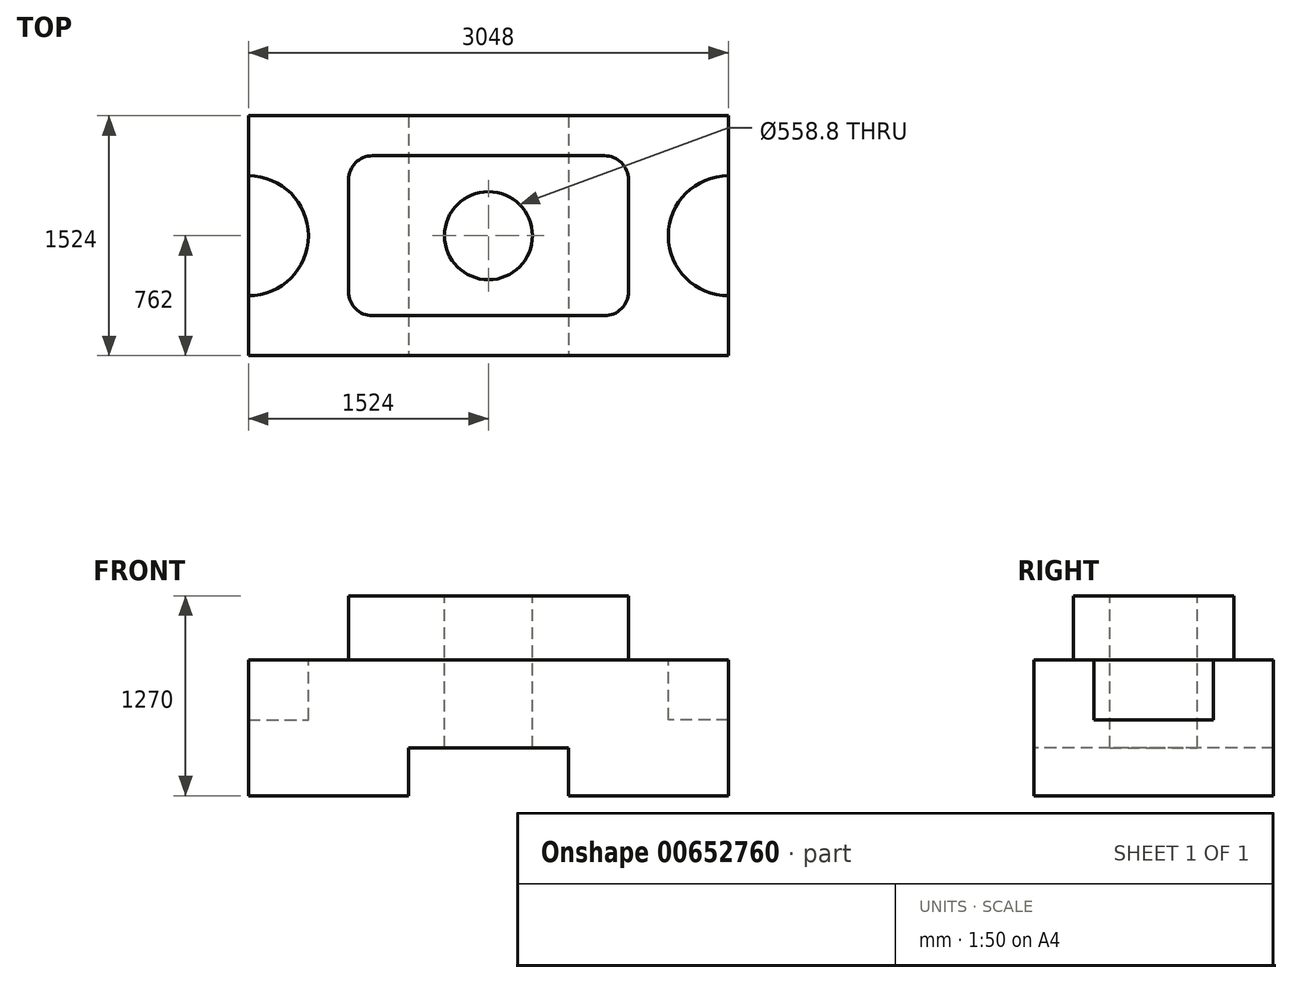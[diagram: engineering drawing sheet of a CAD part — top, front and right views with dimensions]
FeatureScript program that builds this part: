
annotation { "Feature Type Name" : "Feature", "Feature Type Description" : "" }
export const myFeature = defineFeature(function(context is Context, id is Id, definition is map)
    precondition{}
    {
        {
            var Q0;
            Q0=qCreatedBy(makeId("Top.planeOp"),FACE);
            var sketch = newSketch(context, id + "F0", { "sketchPlane" : qUnion([Q0])});
            skLineSegment(sketch, "E0.bottom", {"start": v(1524, -762) * mm, "end": v(-1524, -762) * mm});
            skLineSegment(sketch, "E0.top", {"start": v(1524, 762) * mm, "end": v(-1524, 762) * mm});
            skLineSegment(sketch, "E0.left", {"start": v(1524, -762) * mm, "end": v(1524, 762) * mm});
            skLineSegment(sketch, "E0.right", {"start": v(-1524, -762) * mm, "end": v(-1524, 762) * mm});
            skPoint(sketch, "E0.middle", {"position": v(0, 0) * mm});
            skSolve(sketch);
        }
        {
            var Q0;
            Q0=makeQuery(id+"F0.imprint","IMPRINT",FACE,{"disambiguationData":[TD([[makeQuery(id+"F0.imprint","IMPRINT",EDGE,{"derivedFrom":sQuery(id+"F0.wireOp",EDGE,"E0.bottom")}),-1.0]])]});
            extrude(context, id + "F1", {"entities" : qUnion([Q0]), "depth" : 863.6 * mm, "offsetDistance" : 25.4 * mm});
        }
        {
            var Q0;
            Q0=makeQuery(id+"F1.opExtrude","CAP_FACE",FACE,{"disambiguationData":[OSD([sQuery(id+"F0.wireOp",EDGE,"E0.bottom"),sQuery(id+"F0.wireOp",EDGE,"E0.top"),sQuery(id+"F0.wireOp",EDGE,"E0.left"),sQuery(id+"F0.wireOp",EDGE,"E0.right")])],"isStart":false});
            var sketch = newSketch(context, id + "F2", { "sketchPlane" : qUnion([Q0])});
            skLineSegment(sketch, "E1.bottom", {"start": v(736.6, -508) * mm, "end": v(-736.6, -508) * mm});
            skLineSegment(sketch, "E1.top", {"start": v(736.6, 508) * mm, "end": v(-736.6, 508) * mm});
            skLineSegment(sketch, "E1.left", {"start": v(889, -355.6) * mm, "end": v(889, 355.6) * mm});
            skLineSegment(sketch, "E1.right", {"start": v(-889, -355.6) * mm, "end": v(-889, 355.6) * mm});
            skPoint(sketch, "E1.middle", {"position": v(0, 0) * mm});
            skPoint(sketch, "E2.visualSharp", {"position": v(-889, 508) * mm});
            skArc(sketch, "E2.filletArc", {"start": v(-736.6, 508) * mm, "mid": v(-844.36, 463.36) * mm, "end": v(-889, 355.6) * mm});
            skPoint(sketch, "E3.visualSharp", {"position": v(-889, -508) * mm});
            skArc(sketch, "E3.filletArc", {"start": v(-889, -355.6) * mm, "mid": v(-844.36, -463.36) * mm, "end": v(-736.6, -508) * mm});
            skPoint(sketch, "E4.visualSharp", {"position": v(889, -508) * mm});
            skArc(sketch, "E4.filletArc", {"start": v(736.6, -508) * mm, "mid": v(844.36, -463.36) * mm, "end": v(889, -355.6) * mm});
            skPoint(sketch, "E5.visualSharp", {"position": v(889, 508) * mm});
            skArc(sketch, "E5.filletArc", {"start": v(889, 355.6) * mm, "mid": v(844.36, 463.36) * mm, "end": v(736.6, 508) * mm});
            skSolve(sketch);
        }
        {
            var Q0;
            Q0=makeQuery(id+"F2.imprint","IMPRINT",FACE,{"disambiguationData":[TD([[makeQuery(id+"F2.imprint","IMPRINT",EDGE,{"derivedFrom":sQuery(id+"F2.wireOp",EDGE,"E1.bottom")}),-1.0]])]});
            extrude(context, id + "F3", {"entities" : qUnion([Q0]), "operationType" : NewBodyOperationType.ADD, "depth" : 406.4 * mm, "offsetDistance" : 25.4 * mm});
        }
        {
            var Q0;
            Q0=makeQuery(id+"F3.opExtrude","CAP_FACE",FACE,{"disambiguationData":[OSD([sQuery(id+"F2.wireOp",EDGE,"E1.bottom"),sQuery(id+"F2.wireOp",EDGE,"E1.top"),sQuery(id+"F2.wireOp",EDGE,"E1.left"),sQuery(id+"F2.wireOp",EDGE,"E1.right"),sQuery(id+"F2.wireOp",EDGE,"E2.filletArc"),sQuery(id+"F2.wireOp",EDGE,"E3.filletArc"),sQuery(id+"F2.wireOp",EDGE,"E4.filletArc"),sQuery(id+"F2.wireOp",EDGE,"E5.filletArc")])],"isStart":false});
            var sketch = newSketch(context, id + "F4", { "sketchPlane" : qUnion([Q0])});
            skCircle(sketch, "E6", {"center": v(0, 0) * mm, "radius": 279.4 * mm});
            skSolve(sketch);
        }
        {
            var Q0;
            Q0=makeQuery(id+"F4.imprint","IMPRINT",FACE,{"disambiguationData":[TD([[makeQuery(id+"F4.imprint","IMPRINT",EDGE,{"derivedFrom":sQuery(id+"F4.wireOp",EDGE,"E6")}),1.0]])]});
            extrude(context, id + "F5", {"entities" : qUnion([Q0]), "operationType" : NewBodyOperationType.REMOVE, "endBound" : BoundingType.THROUGH_ALL, "oppositeDirection" : true, "depth" : 25.4 * mm, "offsetDistance" : 25.4 * mm});
        }
        {
            var Q0;
            Q0=makeQuery(id+"F1.opExtrude","CAP_FACE",FACE,{"disambiguationData":[OSD([sQuery(id+"F0.wireOp",EDGE,"E0.bottom"),sQuery(id+"F0.wireOp",EDGE,"E0.top"),sQuery(id+"F0.wireOp",EDGE,"E0.left"),sQuery(id+"F0.wireOp",EDGE,"E0.right")])],"isStart":false});
            var sketch = newSketch(context, id + "F6", { "sketchPlane" : qUnion([Q0])});
            skArc(sketch, "E7", {"start": v(-1524, -381) * mm, "mid": v(-1143, 0) * mm, "end": v(-1524, 381) * mm});
            skArc(sketch, "E8", {"start": v(1524, 381) * mm, "mid": v(1143, 0) * mm, "end": v(1524, -381) * mm});
            skLineSegment(sketch, "E9", {"start": v(-1524, 381) * mm, "end": v(-1524, -381) * mm});
            skLineSegment(sketch, "E10", {"start": v(1524, 381) * mm, "end": v(1524, -381) * mm});
            skSolve(sketch);
        }
        {
            var Q0;
            Q0=makeQuery(id+"F6.imprint","IMPRINT",FACE,{"disambiguationData":[TD([[makeQuery(id+"F6.imprint","IMPRINT",EDGE,{"derivedFrom":sQuery(id+"F6.wireOp",EDGE,"E7")}),1.0]])]});
            var Q1;
            Q1=makeQuery(id+"F6.imprint","IMPRINT",FACE,{"disambiguationData":[TD([[makeQuery(id+"F6.imprint","IMPRINT",EDGE,{"derivedFrom":sQuery(id+"F6.wireOp",EDGE,"E8")}),1.0]])]});
            extrude(context, id + "F7", {"entities" : qUnion([Q0, Q1]), "operationType" : NewBodyOperationType.REMOVE, "oppositeDirection" : true, "depth" : 381 * mm, "offsetDistance" : 25.4 * mm});
        }
        {
            var Q0;
            Q0=makeQuery(id+"F1.opExtrude","SWEPT_FACE",FACE,{"disambiguationData":[OSD([sQuery(id+"F0.wireOp",EDGE,"E0.bottom")])]});
            var sketch = newSketch(context, id + "F8", { "sketchPlane" : qUnion([Q0])});
            skLineSegment(sketch, "E11.top", {"start": v(508, 304.8) * mm, "end": v(-508, 304.8) * mm});
            skLineSegment(sketch, "E11.left", {"start": v(508, 0) * mm, "end": v(508, 304.8) * mm});
            skLineSegment(sketch, "E11.right", {"start": v(-508, 0) * mm, "end": v(-508, 304.8) * mm});
            skPoint(sketch, "E11.middle", {"position": v(0, 0) * mm});
            skLineSegment(sketch, "E12", {"start": v(-508, 0) * mm, "end": v(508, 0) * mm});
            skPoint(sketch, "E11.bottom.start.orphan", {"position": v(508, -304.8) * mm});
            skPoint(sketch, "E13.orphan", {"position": v(-508, -304.8) * mm});
            skSolve(sketch);
        }
        {
            var Q0;
            Q0=makeQuery(id+"F8.imprint","IMPRINT",FACE,{"disambiguationData":[TD([[makeQuery(id+"F8.imprint","IMPRINT",EDGE,{"derivedFrom":sQuery(id+"F8.wireOp",EDGE,"E11.top")}),1.0]])]});
            extrude(context, id + "F9", {"entities" : qUnion([Q0]), "operationType" : NewBodyOperationType.REMOVE, "endBound" : BoundingType.THROUGH_ALL, "oppositeDirection" : true, "depth" : 25.4 * mm, "offsetDistance" : 25.4 * mm});
        }
    });
